# Revit family: NEST_Surface_VIZULO
name_source: partatom
category: Lighting Fixtures
units: mm (PartAtom-declared; Revit-internal decimal feet)

## family parameters
Always vertical = Yes
Cut with Voids When Loaded = No
Light Source = Yes
OmniClass Number = 23.80.70.00
OmniClass Title = Lighting
Part Type = Normal
Room Calculation Point = No
Round Connector Dimension = Use Diameter
Shared = No
Work Plane-Based = No

## types (12) — shared parameters
Color Filter = 16777215
Dimming Lamp Color Temperature Shift = <None>
Emit Shape Visible in Rendering = No
Light Source Symbol Length = 3048 mm  [stored 10 ft]
Spot Beam Angle = 25.00°
Spot Field Angle = 55.00°
Tilt Angle = 90.00°
zero-valued in all types: Default Elevation

## per-type parameters (varying)
| type | Emit from Circle Diameter |
| Diameter 140, 15 W, 3000 K | 61 mm  [stored 0.200131 ft] |
| Diameter 160, 15 W, 3000 K | 81 mm  [stored 0.265748 ft] |
| Diameter 180, 20 W, 3000 K | 101 mm  [stored 0.331365 ft] |
| Diameter 200, 25 W, 3000 K | 121 mm  [stored 0.396982 ft] |
| Diameter 220, 25 W, 3000 K | 141 mm |
| Diameter 140, 15 W, 4000 K | 61 mm  [stored 0.200131 ft] |
| Diameter 160, 15 W, 4000 K | 81 mm  [stored 0.265748 ft] |
| Diameter 160, 20 W, 3000 K | 81 mm  [stored 0.265748 ft] |
| Diameter 160, 20 W, 4000 K | 81 mm  [stored 0.265748 ft] |
| Diameter 180, 20 W, 4000 K | 101 mm  [stored 0.331365 ft] |
| Diameter 200, 25 W, 4000 K | 121 mm  [stored 0.396982 ft] |
| Diameter 220, 25 W, 4000 K | 141 mm |

note: [stored X ft] marks values corroborated as IEEE doubles in the binary element streams (Revit-internal decimal feet)

## geometry (parser evidence)
native form markers: Sweep x3
no freeform markers — native parametric forms only
